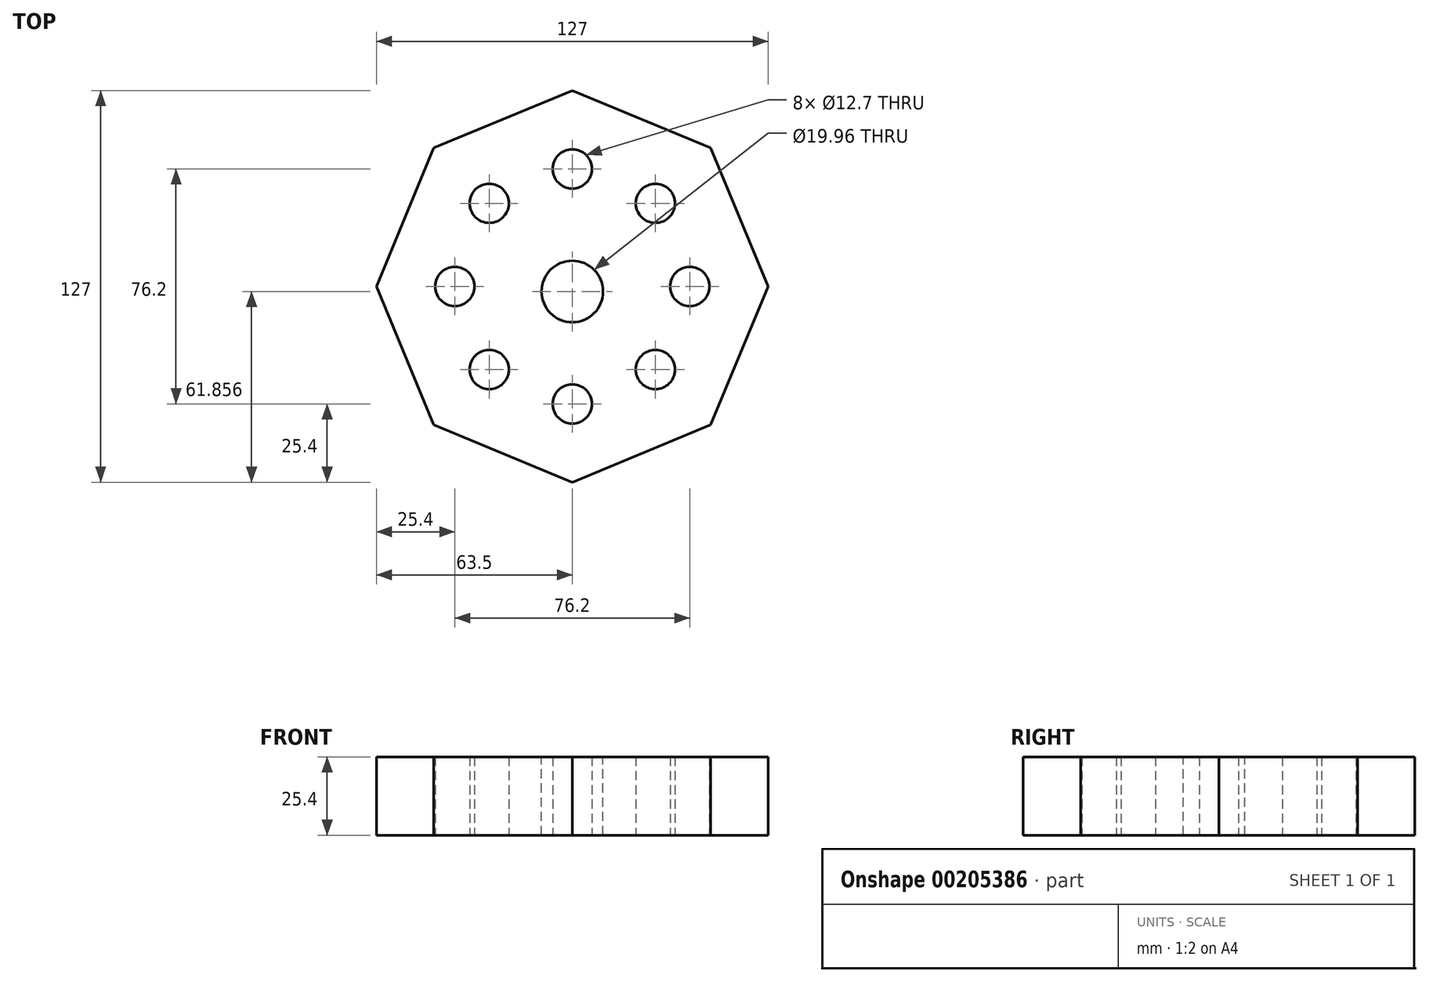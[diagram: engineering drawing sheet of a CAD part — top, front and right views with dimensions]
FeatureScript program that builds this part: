
annotation { "Feature Type Name" : "Feature", "Feature Type Description" : "" }
export const myFeature = defineFeature(function(context is Context, id is Id, definition is map)
    precondition{}
    {
        {
            var Q0;
            Q0=qCreatedBy(makeId("Top.planeOp"),FACE);
            var sketch = newSketch(context, id + "F0", { "sketchPlane" : qUnion([Q0])});
            skCircle(sketch, "E0.cCircle", {"center": v(0, 0) * mm, "radius": 63.5 * mm, "construction": true});
            skLineSegment(sketch, "E0.0", {"start": v(63.5, 0) * mm, "end": v(44.9, -44.9) * mm});
            skLineSegment(sketch, "E0.1", {"start": v(44.9, -44.9) * mm, "end": v(0, -63.5) * mm});
            skLineSegment(sketch, "E0.2", {"start": v(0, -63.5) * mm, "end": v(-44.9, -44.9) * mm});
            skLineSegment(sketch, "E0.3", {"start": v(-44.9, -44.9) * mm, "end": v(-63.5, 0) * mm});
            skLineSegment(sketch, "E0.4", {"start": v(-63.5, 0) * mm, "end": v(-44.9, 44.9) * mm});
            skLineSegment(sketch, "E0.5", {"start": v(-44.9, 44.9) * mm, "end": v(0, 63.5) * mm});
            skLineSegment(sketch, "E0.6", {"start": v(0, 63.5) * mm, "end": v(44.9, 44.9) * mm});
            skLineSegment(sketch, "E0.7", {"start": v(44.9, 44.9) * mm, "end": v(63.5, 0) * mm});
            skCircle(sketch, "E1", {"center": v(38.1, 0) * mm, "radius": 6.35 * mm});
            skCircle(sketch, "E2.1.0", {"center": v(26.94, 26.94) * mm, "radius": 6.35 * mm});
            skCircle(sketch, "E2.2.0", {"center": v(0, 38.1) * mm, "radius": 6.35 * mm});
            skCircle(sketch, "E2.3.0", {"center": v(-26.94, 26.94) * mm, "radius": 6.35 * mm});
            skCircle(sketch, "E2.4.0", {"center": v(-38.1, 0) * mm, "radius": 6.35 * mm});
            skCircle(sketch, "E2.5.0", {"center": v(-26.94, -26.94) * mm, "radius": 6.35 * mm});
            skCircle(sketch, "E2.6.0", {"center": v(0, -38.1) * mm, "radius": 6.35 * mm});
            skCircle(sketch, "E2.7.0", {"center": v(26.94, -26.94) * mm, "radius": 6.35 * mm});
            skSolve(sketch);
        }
        {
            var Q0;
            Q0 = qSketchRegion(id + "F0", true);
            extrude(context, id + "F1", {"entities" : qUnion([Q0]), "depth" : 25.4 * mm});
        }
        {
            var Q0;
            Q0=makeQuery(id+"F1.opExtrude","CAP_FACE",FACE,{"disambiguationData":[OSD([sQuery(id+"F0.wireOp",EDGE,"E0.0"),sQuery(id+"F0.wireOp",EDGE,"E0.1"),sQuery(id+"F0.wireOp",EDGE,"E0.2"),sQuery(id+"F0.wireOp",EDGE,"E0.3"),sQuery(id+"F0.wireOp",EDGE,"E0.4"),sQuery(id+"F0.wireOp",EDGE,"E0.5"),sQuery(id+"F0.wireOp",EDGE,"E0.6"),sQuery(id+"F0.wireOp",EDGE,"E0.7"),sQuery(id+"F0.wireOp",EDGE,"E1"),sQuery(id+"F0.wireOp",EDGE,"E2.1.0"),sQuery(id+"F0.wireOp",EDGE,"E2.2.0"),sQuery(id+"F0.wireOp",EDGE,"E2.3.0"),sQuery(id+"F0.wireOp",EDGE,"E2.4.0"),sQuery(id+"F0.wireOp",EDGE,"E2.5.0"),sQuery(id+"F0.wireOp",EDGE,"E2.6.0"),sQuery(id+"F0.wireOp",EDGE,"E2.7.0")])],"isStart":false});
            var sketch = newSketch(context, id + "F2", { "sketchPlane" : qUnion([Q0])});
            skCircle(sketch, "E3", {"center": v(0, -1.64) * mm, "radius": 9.98 * mm});
            skSolve(sketch);
        }
        {
            var Q0;
            Q0 = qSketchRegion(id + "F2", true);
            extrude(context, id + "F3", {"entities" : qUnion([Q0]), "operationType" : NewBodyOperationType.REMOVE, "oppositeDirection" : true, "depth" : 25.4 * mm});
        }
    });
